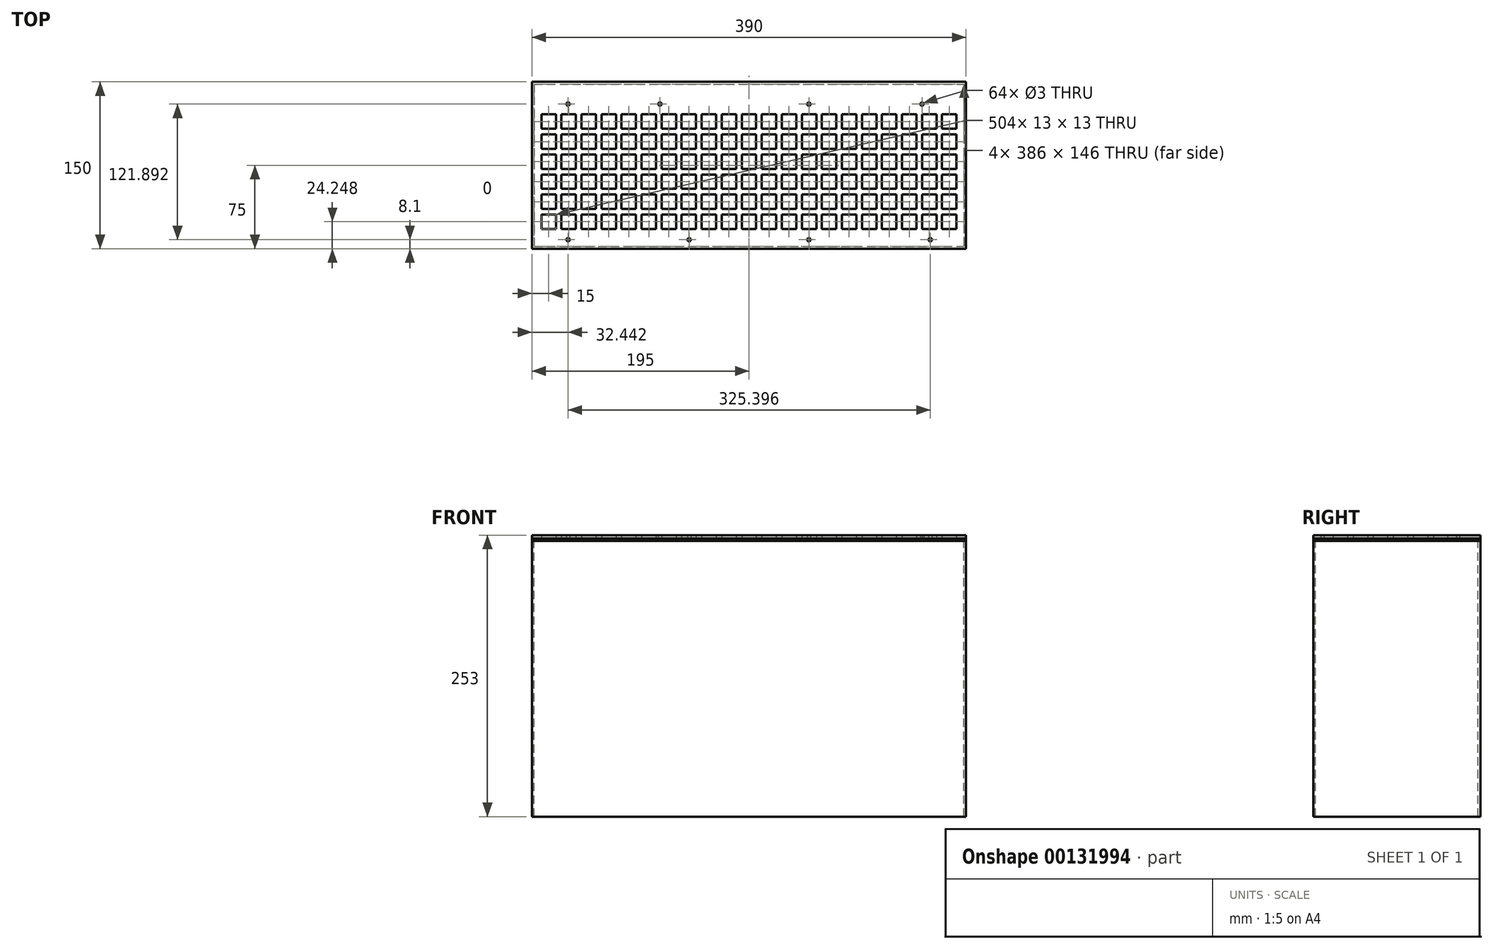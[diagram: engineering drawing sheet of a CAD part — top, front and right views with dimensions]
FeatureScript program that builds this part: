
annotation { "Feature Type Name" : "Feature", "Feature Type Description" : "" }
export const myFeature = defineFeature(function(context is Context, id is Id, definition is map)
    precondition{}
    {
        {
            var Q0;
            Q0=qCreatedBy(makeId("Top.planeOp"),FACE);
            var sketch = newSketch(context, id + "F0", { "sketchPlane" : qUnion([Q0])});
            skLineSegment(sketch, "E0.bottom", {"start": v(0, 0) * mm, "end": v(390, 0) * mm});
            skLineSegment(sketch, "E0.top", {"start": v(0, -150) * mm, "end": v(390, -150) * mm});
            skLineSegment(sketch, "E0.left", {"start": v(0, 0) * mm, "end": v(0, -150) * mm});
            skLineSegment(sketch, "E0.right", {"start": v(390, 0) * mm, "end": v(390, -150) * mm});
            skLineSegment(sketch, "E1.bottom", {"start": v(8.5, -29.25) * mm, "end": v(21.5, -29.25) * mm});
            skLineSegment(sketch, "E1.top", {"start": v(8.5, -42.25) * mm, "end": v(21.5, -42.25) * mm});
            skLineSegment(sketch, "E1.left", {"start": v(8.5, -29.25) * mm, "end": v(8.5, -42.25) * mm});
            skLineSegment(sketch, "E1.right", {"start": v(21.5, -29.25) * mm, "end": v(21.5, -42.25) * mm});
            skLineSegment(sketch, "E2.bottom", {"start": v(8.5, -47.25) * mm, "end": v(21.5, -47.25) * mm});
            skLineSegment(sketch, "E2.top", {"start": v(8.5, -60.25) * mm, "end": v(21.5, -60.25) * mm});
            skLineSegment(sketch, "E2.left", {"start": v(8.5, -47.25) * mm, "end": v(8.5, -60.25) * mm});
            skLineSegment(sketch, "E2.right", {"start": v(21.5, -47.25) * mm, "end": v(21.5, -60.25) * mm});
            skLineSegment(sketch, "E3.bottom", {"start": v(8.5, -65.25) * mm, "end": v(21.5, -65.25) * mm});
            skLineSegment(sketch, "E3.top", {"start": v(8.5, -78.25) * mm, "end": v(21.5, -78.25) * mm});
            skLineSegment(sketch, "E3.left", {"start": v(8.5, -65.25) * mm, "end": v(8.5, -78.25) * mm});
            skLineSegment(sketch, "E3.right", {"start": v(21.5, -65.25) * mm, "end": v(21.5, -78.25) * mm});
            skLineSegment(sketch, "E4.bottom", {"start": v(8.5, -83.25) * mm, "end": v(21.5, -83.25) * mm});
            skLineSegment(sketch, "E4.top", {"start": v(8.5, -96.25) * mm, "end": v(21.5, -96.25) * mm});
            skLineSegment(sketch, "E4.left", {"start": v(8.5, -83.25) * mm, "end": v(8.5, -96.25) * mm});
            skLineSegment(sketch, "E4.right", {"start": v(21.5, -83.25) * mm, "end": v(21.5, -96.25) * mm});
            skLineSegment(sketch, "E5.bottom", {"start": v(8.5, -101.25) * mm, "end": v(21.5, -101.25) * mm});
            skLineSegment(sketch, "E5.top", {"start": v(8.5, -114.25) * mm, "end": v(21.5, -114.25) * mm});
            skLineSegment(sketch, "E5.left", {"start": v(8.5, -101.25) * mm, "end": v(8.5, -114.25) * mm});
            skLineSegment(sketch, "E5.right", {"start": v(21.5, -101.25) * mm, "end": v(21.5, -114.25) * mm});
            skLineSegment(sketch, "E6.bottom", {"start": v(8.5, -119.25) * mm, "end": v(21.5, -119.25) * mm});
            skLineSegment(sketch, "E6.top", {"start": v(8.5, -132.25) * mm, "end": v(21.5, -132.25) * mm});
            skLineSegment(sketch, "E6.left", {"start": v(8.5, -119.25) * mm, "end": v(8.5, -132.25) * mm});
            skLineSegment(sketch, "E6.right", {"start": v(21.5, -119.25) * mm, "end": v(21.5, -132.25) * mm});
            skLineSegment(sketch, "E7", {"start": v(24, -21.56) * mm, "end": v(24, -144.75) * mm, "construction": true});
            skLineSegment(sketch, "E8.MirrorCS", {"start": v(39.5, -47.25) * mm, "end": v(39.5, -60.25) * mm});
            skLineSegment(sketch, "E9.MirrorCS", {"start": v(39.5, -60.25) * mm, "end": v(26.5, -60.25) * mm});
            skLineSegment(sketch, "E10.MirrorCS", {"start": v(39.5, -132.25) * mm, "end": v(26.5, -132.25) * mm});
            skLineSegment(sketch, "E11.MirrorCS", {"start": v(39.5, -119.25) * mm, "end": v(26.5, -119.25) * mm});
            skLineSegment(sketch, "E12.MirrorCS", {"start": v(39.5, -119.25) * mm, "end": v(39.5, -132.25) * mm});
            skLineSegment(sketch, "E13.MirrorCS", {"start": v(26.5, -29.25) * mm, "end": v(26.5, -42.25) * mm});
            skLineSegment(sketch, "E14.MirrorCS", {"start": v(39.5, -29.25) * mm, "end": v(26.5, -29.25) * mm});
            skLineSegment(sketch, "E15.MirrorCS", {"start": v(39.5, -101.25) * mm, "end": v(26.5, -101.25) * mm});
            skLineSegment(sketch, "E16.MirrorCS", {"start": v(26.5, -83.25) * mm, "end": v(26.5, -96.25) * mm});
            skLineSegment(sketch, "E17.MirrorCS", {"start": v(39.5, -83.25) * mm, "end": v(39.5, -96.25) * mm});
            skLineSegment(sketch, "E18.MirrorCS", {"start": v(39.5, -96.25) * mm, "end": v(26.5, -96.25) * mm});
            skLineSegment(sketch, "E19.MirrorCS", {"start": v(39.5, -83.25) * mm, "end": v(26.5, -83.25) * mm});
            skLineSegment(sketch, "E20.MirrorCS", {"start": v(26.5, -65.25) * mm, "end": v(26.5, -78.25) * mm});
            skLineSegment(sketch, "E21.MirrorCS", {"start": v(39.5, -65.25) * mm, "end": v(39.5, -78.25) * mm});
            skLineSegment(sketch, "E22.MirrorCS", {"start": v(39.5, -65.25) * mm, "end": v(26.5, -65.25) * mm});
            skLineSegment(sketch, "E23.MirrorCS", {"start": v(39.5, -78.25) * mm, "end": v(26.5, -78.25) * mm});
            skLineSegment(sketch, "E24.MirrorCS", {"start": v(26.5, -101.25) * mm, "end": v(26.5, -114.25) * mm});
            skLineSegment(sketch, "E25.MirrorCS", {"start": v(26.5, -47.25) * mm, "end": v(26.5, -60.25) * mm});
            skLineSegment(sketch, "E26.MirrorCS", {"start": v(26.5, -119.25) * mm, "end": v(26.5, -132.25) * mm});
            skLineSegment(sketch, "E27.MirrorCS", {"start": v(39.5, -101.25) * mm, "end": v(39.5, -114.25) * mm});
            skLineSegment(sketch, "E28.MirrorCS", {"start": v(39.5, -29.25) * mm, "end": v(39.5, -42.25) * mm});
            skLineSegment(sketch, "E29.MirrorCS", {"start": v(39.5, -114.25) * mm, "end": v(26.5, -114.25) * mm});
            skLineSegment(sketch, "E30.MirrorCS", {"start": v(39.5, -47.25) * mm, "end": v(26.5, -47.25) * mm});
            skLineSegment(sketch, "E31.MirrorCS", {"start": v(39.5, -42.25) * mm, "end": v(26.5, -42.25) * mm});
            skLineSegment(sketch, "E32", {"start": v(42, -21.56) * mm, "end": v(42, -144.75) * mm, "construction": true});
            skLineSegment(sketch, "E33.MirrorCS", {"start": v(57.5, -119.25) * mm, "end": v(57.5, -132.25) * mm});
            skLineSegment(sketch, "E34.MirrorCS", {"start": v(44.5, -29.25) * mm, "end": v(44.5, -42.25) * mm});
            skLineSegment(sketch, "E35.MirrorCS", {"start": v(44.5, -119.25) * mm, "end": v(44.5, -132.25) * mm});
            skLineSegment(sketch, "E36.MirrorCS", {"start": v(44.5, -114.25) * mm, "end": v(57.5, -114.25) * mm});
            skLineSegment(sketch, "E37.MirrorCS", {"start": v(75.5, -83.25) * mm, "end": v(75.5, -96.25) * mm});
            skLineSegment(sketch, "E38.MirrorCS", {"start": v(62.5, -65.25) * mm, "end": v(62.5, -78.25) * mm});
            skLineSegment(sketch, "E39.MirrorCS", {"start": v(75.5, -114.25) * mm, "end": v(62.5, -114.25) * mm});
            skLineSegment(sketch, "E40.MirrorCS", {"start": v(75.5, -42.25) * mm, "end": v(62.5, -42.25) * mm});
            skLineSegment(sketch, "E41.MirrorCS", {"start": v(57.5, -83.25) * mm, "end": v(57.5, -96.25) * mm});
            skLineSegment(sketch, "E42.MirrorCS", {"start": v(75.5, -101.25) * mm, "end": v(75.5, -114.25) * mm});
            skLineSegment(sketch, "E43.MirrorCS", {"start": v(75.5, -29.25) * mm, "end": v(75.5, -42.25) * mm});
            skLineSegment(sketch, "E44.MirrorCS", {"start": v(44.5, -83.25) * mm, "end": v(44.5, -96.25) * mm});
            skLineSegment(sketch, "E45.MirrorCS", {"start": v(44.5, -96.25) * mm, "end": v(57.5, -96.25) * mm});
            skLineSegment(sketch, "E46.MirrorCS", {"start": v(62.5, -101.25) * mm, "end": v(62.5, -114.25) * mm});
            skLineSegment(sketch, "E47.MirrorCS", {"start": v(62.5, -29.25) * mm, "end": v(62.5, -42.25) * mm});
            skLineSegment(sketch, "E48.MirrorCS", {"start": v(44.5, -83.25) * mm, "end": v(57.5, -83.25) * mm});
            skLineSegment(sketch, "E49.MirrorCS", {"start": v(75.5, -119.25) * mm, "end": v(62.5, -119.25) * mm});
            skLineSegment(sketch, "E50.MirrorCS", {"start": v(75.5, -47.25) * mm, "end": v(62.5, -47.25) * mm});
            skLineSegment(sketch, "E51.MirrorCS", {"start": v(57.5, -65.25) * mm, "end": v(57.5, -78.25) * mm});
            skLineSegment(sketch, "E52.MirrorCS", {"start": v(75.5, -60.25) * mm, "end": v(62.5, -60.25) * mm});
            skLineSegment(sketch, "E53.MirrorCS", {"start": v(75.5, -132.25) * mm, "end": v(62.5, -132.25) * mm});
            skLineSegment(sketch, "E54.MirrorCS", {"start": v(44.5, -132.25) * mm, "end": v(57.5, -132.25) * mm});
            skLineSegment(sketch, "E55.MirrorCS", {"start": v(75.5, -78.25) * mm, "end": v(62.5, -78.25) * mm});
            skLineSegment(sketch, "E56.MirrorCS", {"start": v(57.5, -101.25) * mm, "end": v(57.5, -114.25) * mm});
            skLineSegment(sketch, "E57.MirrorCS", {"start": v(44.5, -47.25) * mm, "end": v(44.5, -60.25) * mm});
            skLineSegment(sketch, "E58.MirrorCS", {"start": v(44.5, -65.25) * mm, "end": v(44.5, -78.25) * mm});
            skLineSegment(sketch, "E59.MirrorCS", {"start": v(75.5, -119.25) * mm, "end": v(75.5, -132.25) * mm});
            skLineSegment(sketch, "E60.MirrorCS", {"start": v(75.5, -47.25) * mm, "end": v(75.5, -60.25) * mm});
            skLineSegment(sketch, "E61.MirrorCS", {"start": v(75.5, -65.25) * mm, "end": v(75.5, -78.25) * mm});
            skLineSegment(sketch, "E62.MirrorCS", {"start": v(57.5, -47.25) * mm, "end": v(57.5, -60.25) * mm});
            skLineSegment(sketch, "E63.MirrorCS", {"start": v(44.5, -60.25) * mm, "end": v(57.5, -60.25) * mm});
            skLineSegment(sketch, "E64.MirrorCS", {"start": v(44.5, -65.25) * mm, "end": v(57.5, -65.25) * mm});
            skLineSegment(sketch, "E65.MirrorCS", {"start": v(62.5, -119.25) * mm, "end": v(62.5, -132.25) * mm});
            skLineSegment(sketch, "E66.MirrorCS", {"start": v(62.5, -47.25) * mm, "end": v(62.5, -60.25) * mm});
            skLineSegment(sketch, "E67.MirrorCS", {"start": v(44.5, -119.25) * mm, "end": v(57.5, -119.25) * mm});
            skLineSegment(sketch, "E68.MirrorCS", {"start": v(44.5, -101.25) * mm, "end": v(44.5, -114.25) * mm});
            skLineSegment(sketch, "E69.MirrorCS", {"start": v(75.5, -83.25) * mm, "end": v(62.5, -83.25) * mm});
            skLineSegment(sketch, "E70.MirrorCS", {"start": v(44.5, -101.25) * mm, "end": v(57.5, -101.25) * mm});
            skLineSegment(sketch, "E71.MirrorCS", {"start": v(75.5, -96.25) * mm, "end": v(62.5, -96.25) * mm});
            skLineSegment(sketch, "E72.MirrorCS", {"start": v(44.5, -78.25) * mm, "end": v(57.5, -78.25) * mm});
            skLineSegment(sketch, "E73.MirrorCS", {"start": v(75.5, -65.25) * mm, "end": v(62.5, -65.25) * mm});
            skLineSegment(sketch, "E74.MirrorCS", {"start": v(44.5, -42.25) * mm, "end": v(57.5, -42.25) * mm});
            skLineSegment(sketch, "E75.MirrorCS", {"start": v(44.5, -47.25) * mm, "end": v(57.5, -47.25) * mm});
            skLineSegment(sketch, "E76.MirrorCS", {"start": v(62.5, -83.25) * mm, "end": v(62.5, -96.25) * mm});
            skLineSegment(sketch, "E77.MirrorCS", {"start": v(75.5, -29.25) * mm, "end": v(62.5, -29.25) * mm});
            skLineSegment(sketch, "E78.MirrorCS", {"start": v(44.5, -29.25) * mm, "end": v(57.5, -29.25) * mm});
            skLineSegment(sketch, "E79.MirrorCS", {"start": v(75.5, -101.25) * mm, "end": v(62.5, -101.25) * mm});
            skLineSegment(sketch, "E80.MirrorCS", {"start": v(57.5, -29.25) * mm, "end": v(57.5, -42.25) * mm});
            skLineSegment(sketch, "E81", {"start": v(78, -21.56) * mm, "end": v(78, -144.75) * mm, "construction": true});
            skLineSegment(sketch, "E82.MirrorCS", {"start": v(111.5, -29.25) * mm, "end": v(111.5, -42.25) * mm});
            skLineSegment(sketch, "E83.MirrorCS", {"start": v(116.5, -83.25) * mm, "end": v(116.5, -96.25) * mm});
            skLineSegment(sketch, "E84.MirrorCS", {"start": v(93.5, -119.25) * mm, "end": v(93.5, -132.25) * mm});
            skLineSegment(sketch, "E85.MirrorCS", {"start": v(147.5, -47.25) * mm, "end": v(134.5, -47.25) * mm});
            skLineSegment(sketch, "E86.MirrorCS", {"start": v(147.5, -101.25) * mm, "end": v(134.5, -101.25) * mm});
            skLineSegment(sketch, "E87.MirrorCS", {"start": v(147.5, -29.25) * mm, "end": v(134.5, -29.25) * mm});
            skLineSegment(sketch, "E88.MirrorCS", {"start": v(147.5, -119.25) * mm, "end": v(134.5, -119.25) * mm});
            skLineSegment(sketch, "E89.MirrorCS", {"start": v(116.5, -83.25) * mm, "end": v(129.5, -83.25) * mm});
            skLineSegment(sketch, "E90.MirrorCS", {"start": v(111.5, -119.25) * mm, "end": v(111.5, -132.25) * mm});
            skLineSegment(sketch, "E91.MirrorCS", {"start": v(98.5, -29.25) * mm, "end": v(98.5, -42.25) * mm});
            skLineSegment(sketch, "E92.MirrorCS", {"start": v(129.5, -83.25) * mm, "end": v(129.5, -96.25) * mm});
            skLineSegment(sketch, "E93.MirrorCS", {"start": v(147.5, -65.25) * mm, "end": v(147.5, -78.25) * mm});
            skLineSegment(sketch, "E94.MirrorCS", {"start": v(116.5, -29.25) * mm, "end": v(129.5, -29.25) * mm});
            skLineSegment(sketch, "E95.MirrorCS", {"start": v(116.5, -47.25) * mm, "end": v(129.5, -47.25) * mm});
            skLineSegment(sketch, "E96.MirrorCS", {"start": v(93.5, -101.25) * mm, "end": v(93.5, -114.25) * mm});
            skLineSegment(sketch, "E97.MirrorCS", {"start": v(98.5, -47.25) * mm, "end": v(98.5, -60.25) * mm});
            skLineSegment(sketch, "E98.MirrorCS", {"start": v(93.5, -47.25) * mm, "end": v(93.5, -60.25) * mm});
            skLineSegment(sketch, "E99.MirrorCS", {"start": v(134.5, -83.25) * mm, "end": v(134.5, -96.25) * mm});
            skLineSegment(sketch, "E100.MirrorCS", {"start": v(111.5, -29.25) * mm, "end": v(98.5, -29.25) * mm});
            skLineSegment(sketch, "E101.MirrorCS", {"start": v(80.5, -29.25) * mm, "end": v(93.5, -29.25) * mm});
            skLineSegment(sketch, "E102.MirrorCS", {"start": v(129.5, -29.25) * mm, "end": v(129.5, -42.25) * mm});
            skLineSegment(sketch, "E103.MirrorCS", {"start": v(116.5, -114.25) * mm, "end": v(129.5, -114.25) * mm});
            skLineSegment(sketch, "E104.MirrorCS", {"start": v(111.5, -96.25) * mm, "end": v(98.5, -96.25) * mm});
            skLineSegment(sketch, "E105.MirrorCS", {"start": v(80.5, -65.25) * mm, "end": v(80.5, -78.25) * mm});
            skLineSegment(sketch, "E106.MirrorCS", {"start": v(93.5, -83.25) * mm, "end": v(93.5, -96.25) * mm});
            skLineSegment(sketch, "E107.MirrorCS", {"start": v(116.5, -119.25) * mm, "end": v(116.5, -132.25) * mm});
            skLineSegment(sketch, "E108.MirrorCS", {"start": v(116.5, -29.25) * mm, "end": v(116.5, -42.25) * mm});
            skLineSegment(sketch, "E109.MirrorCS", {"start": v(111.5, -83.25) * mm, "end": v(111.5, -96.25) * mm});
            skLineSegment(sketch, "E110.MirrorCS", {"start": v(80.5, -47.25) * mm, "end": v(80.5, -60.25) * mm});
            skLineSegment(sketch, "E111.MirrorCS", {"start": v(147.5, -96.25) * mm, "end": v(134.5, -96.25) * mm});
            skLineSegment(sketch, "E112.MirrorCS", {"start": v(134.5, -29.25) * mm, "end": v(134.5, -42.25) * mm});
            skLineSegment(sketch, "E113.MirrorCS", {"start": v(80.5, -132.25) * mm, "end": v(93.5, -132.25) * mm});
            skLineSegment(sketch, "E114.MirrorCS", {"start": v(80.5, -83.25) * mm, "end": v(93.5, -83.25) * mm});
            skLineSegment(sketch, "E115.MirrorCS", {"start": v(147.5, -47.25) * mm, "end": v(147.5, -60.25) * mm});
            skLineSegment(sketch, "E116.MirrorCS", {"start": v(147.5, -119.25) * mm, "end": v(147.5, -132.25) * mm});
            skLineSegment(sketch, "E117.MirrorCS", {"start": v(116.5, -65.25) * mm, "end": v(116.5, -78.25) * mm});
            skLineSegment(sketch, "E118.MirrorCS", {"start": v(80.5, -83.25) * mm, "end": v(80.5, -96.25) * mm});
            skLineSegment(sketch, "E119.MirrorCS", {"start": v(134.5, -101.25) * mm, "end": v(134.5, -114.25) * mm});
            skLineSegment(sketch, "E120.MirrorCS", {"start": v(111.5, -47.25) * mm, "end": v(98.5, -47.25) * mm});
            skLineSegment(sketch, "E121.MirrorCS", {"start": v(116.5, -101.25) * mm, "end": v(116.5, -114.25) * mm});
            skLineSegment(sketch, "E122.MirrorCS", {"start": v(116.5, -119.25) * mm, "end": v(129.5, -119.25) * mm});
            skLineSegment(sketch, "E123.MirrorCS", {"start": v(80.5, -29.25) * mm, "end": v(80.5, -42.25) * mm});
            skLineSegment(sketch, "E124.MirrorCS", {"start": v(80.5, -119.25) * mm, "end": v(80.5, -132.25) * mm});
            skLineSegment(sketch, "E125.MirrorCS", {"start": v(147.5, -83.25) * mm, "end": v(134.5, -83.25) * mm});
            skLineSegment(sketch, "E126.MirrorCS", {"start": v(111.5, -42.25) * mm, "end": v(98.5, -42.25) * mm});
            skLineSegment(sketch, "E127.MirrorCS", {"start": v(116.5, -132.25) * mm, "end": v(129.5, -132.25) * mm});
            skLineSegment(sketch, "E128.MirrorCS", {"start": v(129.5, -119.25) * mm, "end": v(129.5, -132.25) * mm});
            skLineSegment(sketch, "E129.MirrorCS", {"start": v(80.5, -101.25) * mm, "end": v(80.5, -114.25) * mm});
            skLineSegment(sketch, "E130.MirrorCS", {"start": v(111.5, -65.25) * mm, "end": v(111.5, -78.25) * mm});
            skLineSegment(sketch, "E131.MirrorCS", {"start": v(80.5, -60.25) * mm, "end": v(93.5, -60.25) * mm});
            skLineSegment(sketch, "E132.MirrorCS", {"start": v(111.5, -101.25) * mm, "end": v(111.5, -114.25) * mm});
            skLineSegment(sketch, "E133.MirrorCS", {"start": v(134.5, -65.25) * mm, "end": v(134.5, -78.25) * mm});
            skLineSegment(sketch, "E134.MirrorCS", {"start": v(147.5, -60.25) * mm, "end": v(134.5, -60.25) * mm});
            skLineSegment(sketch, "E135.MirrorCS", {"start": v(147.5, -132.25) * mm, "end": v(134.5, -132.25) * mm});
            skLineSegment(sketch, "E136.MirrorCS", {"start": v(129.5, -65.25) * mm, "end": v(129.5, -78.25) * mm});
            skLineSegment(sketch, "E137.MirrorCS", {"start": v(111.5, -114.25) * mm, "end": v(98.5, -114.25) * mm});
            skLineSegment(sketch, "E138.MirrorCS", {"start": v(80.5, -65.25) * mm, "end": v(93.5, -65.25) * mm});
            skLineSegment(sketch, "E139.MirrorCS", {"start": v(116.5, -60.25) * mm, "end": v(129.5, -60.25) * mm});
            skLineSegment(sketch, "E140.MirrorCS", {"start": v(129.5, -47.25) * mm, "end": v(129.5, -60.25) * mm});
            skLineSegment(sketch, "E141.MirrorCS", {"start": v(98.5, -83.25) * mm, "end": v(98.5, -96.25) * mm});
            skLineSegment(sketch, "E142.MirrorCS", {"start": v(111.5, -47.25) * mm, "end": v(111.5, -60.25) * mm});
            skLineSegment(sketch, "E143.MirrorCS", {"start": v(80.5, -47.25) * mm, "end": v(93.5, -47.25) * mm});
            skLineSegment(sketch, "E144.MirrorCS", {"start": v(116.5, -96.25) * mm, "end": v(129.5, -96.25) * mm});
            skLineSegment(sketch, "E145.MirrorCS", {"start": v(111.5, -119.25) * mm, "end": v(98.5, -119.25) * mm});
            skLineSegment(sketch, "E146.MirrorCS", {"start": v(98.5, -65.25) * mm, "end": v(98.5, -78.25) * mm});
            skLineSegment(sketch, "E147.MirrorCS", {"start": v(111.5, -60.25) * mm, "end": v(98.5, -60.25) * mm});
            skLineSegment(sketch, "E148.MirrorCS", {"start": v(147.5, -83.25) * mm, "end": v(147.5, -96.25) * mm});
            skLineSegment(sketch, "E149.MirrorCS", {"start": v(111.5, -65.25) * mm, "end": v(98.5, -65.25) * mm});
            skLineSegment(sketch, "E150.MirrorCS", {"start": v(111.5, -83.25) * mm, "end": v(98.5, -83.25) * mm});
            skLineSegment(sketch, "E151.MirrorCS", {"start": v(116.5, -42.25) * mm, "end": v(129.5, -42.25) * mm});
            skLineSegment(sketch, "E152.MirrorCS", {"start": v(147.5, -42.25) * mm, "end": v(134.5, -42.25) * mm});
            skLineSegment(sketch, "E153.MirrorCS", {"start": v(147.5, -114.25) * mm, "end": v(134.5, -114.25) * mm});
            skLineSegment(sketch, "E154.MirrorCS", {"start": v(98.5, -101.25) * mm, "end": v(98.5, -114.25) * mm});
            skLineSegment(sketch, "E155.MirrorCS", {"start": v(80.5, -42.25) * mm, "end": v(93.5, -42.25) * mm});
            skLineSegment(sketch, "E156.MirrorCS", {"start": v(129.5, -101.25) * mm, "end": v(129.5, -114.25) * mm});
            skLineSegment(sketch, "E157.MirrorCS", {"start": v(116.5, -47.25) * mm, "end": v(116.5, -60.25) * mm});
            skLineSegment(sketch, "E158.MirrorCS", {"start": v(111.5, -78.25) * mm, "end": v(98.5, -78.25) * mm});
            skLineSegment(sketch, "E159.MirrorCS", {"start": v(147.5, -101.25) * mm, "end": v(147.5, -114.25) * mm});
            skLineSegment(sketch, "E160.MirrorCS", {"start": v(93.5, -29.25) * mm, "end": v(93.5, -42.25) * mm});
            skLineSegment(sketch, "E161.MirrorCS", {"start": v(116.5, -101.25) * mm, "end": v(129.5, -101.25) * mm});
            skLineSegment(sketch, "E162.MirrorCS", {"start": v(80.5, -101.25) * mm, "end": v(93.5, -101.25) * mm});
            skLineSegment(sketch, "E163.MirrorCS", {"start": v(147.5, -29.25) * mm, "end": v(147.5, -42.25) * mm});
            skLineSegment(sketch, "E164.MirrorCS", {"start": v(80.5, -119.25) * mm, "end": v(93.5, -119.25) * mm});
            skLineSegment(sketch, "E165.MirrorCS", {"start": v(98.5, -119.25) * mm, "end": v(98.5, -132.25) * mm});
            skLineSegment(sketch, "E166.MirrorCS", {"start": v(147.5, -78.25) * mm, "end": v(134.5, -78.25) * mm});
            skLineSegment(sketch, "E167.MirrorCS", {"start": v(147.5, -65.25) * mm, "end": v(134.5, -65.25) * mm});
            skLineSegment(sketch, "E168.MirrorCS", {"start": v(80.5, -78.25) * mm, "end": v(93.5, -78.25) * mm});
            skLineSegment(sketch, "E169.MirrorCS", {"start": v(80.5, -96.25) * mm, "end": v(93.5, -96.25) * mm});
            skLineSegment(sketch, "E170.MirrorCS", {"start": v(116.5, -78.25) * mm, "end": v(129.5, -78.25) * mm});
            skLineSegment(sketch, "E171.MirrorCS", {"start": v(80.5, -114.25) * mm, "end": v(93.5, -114.25) * mm});
            skLineSegment(sketch, "E172.MirrorCS", {"start": v(134.5, -119.25) * mm, "end": v(134.5, -132.25) * mm});
            skLineSegment(sketch, "E173.MirrorCS", {"start": v(116.5, -65.25) * mm, "end": v(129.5, -65.25) * mm});
            skLineSegment(sketch, "E174.MirrorCS", {"start": v(93.5, -65.25) * mm, "end": v(93.5, -78.25) * mm});
            skLineSegment(sketch, "E175.MirrorCS", {"start": v(134.5, -47.25) * mm, "end": v(134.5, -60.25) * mm});
            skLineSegment(sketch, "E176.MirrorCS", {"start": v(111.5, -101.25) * mm, "end": v(98.5, -101.25) * mm});
            skLineSegment(sketch, "E177.MirrorCS", {"start": v(111.5, -132.25) * mm, "end": v(98.5, -132.25) * mm});
            skLineSegment(sketch, "E178", {"start": v(150, -21.56) * mm, "end": v(150, -144.75) * mm, "construction": true});
            skLineSegment(sketch, "E179.MirrorCS", {"start": v(291.5, -83.25) * mm, "end": v(291.5, -96.25) * mm});
            skLineSegment(sketch, "E180.MirrorCS", {"start": v(291.5, -101.25) * mm, "end": v(278.5, -101.25) * mm});
            skLineSegment(sketch, "E181.MirrorCS", {"start": v(291.5, -29.25) * mm, "end": v(278.5, -29.25) * mm});
            skLineSegment(sketch, "E182.MirrorCS", {"start": v(291.5, -29.25) * mm, "end": v(291.5, -42.25) * mm});
            skLineSegment(sketch, "E183.MirrorCS", {"start": v(291.5, -47.25) * mm, "end": v(291.5, -60.25) * mm});
            skLineSegment(sketch, "E184.MirrorCS", {"start": v(291.5, -119.25) * mm, "end": v(291.5, -132.25) * mm});
            skLineSegment(sketch, "E185.MirrorCS", {"start": v(291.5, -65.25) * mm, "end": v(278.5, -65.25) * mm});
            skLineSegment(sketch, "E186.MirrorCS", {"start": v(291.5, -65.25) * mm, "end": v(291.5, -78.25) * mm});
            skLineSegment(sketch, "E187.MirrorCS", {"start": v(260.5, -119.25) * mm, "end": v(260.5, -132.25) * mm});
            skLineSegment(sketch, "E188.MirrorCS", {"start": v(255.5, -83.25) * mm, "end": v(255.5, -96.25) * mm});
            skLineSegment(sketch, "E189.MirrorCS", {"start": v(170.5, -101.25) * mm, "end": v(170.5, -114.25) * mm});
            skLineSegment(sketch, "E190.MirrorCS", {"start": v(224.5, -65.25) * mm, "end": v(224.5, -78.25) * mm});
            skLineSegment(sketch, "E191.MirrorCS", {"start": v(255.5, -96.25) * mm, "end": v(242.5, -96.25) * mm});
            skLineSegment(sketch, "E192.MirrorCS", {"start": v(260.5, -114.25) * mm, "end": v(273.5, -114.25) * mm});
            skLineSegment(sketch, "E193.MirrorCS", {"start": v(273.5, -29.25) * mm, "end": v(273.5, -42.25) * mm});
            skLineSegment(sketch, "E194.MirrorCS", {"start": v(152.5, -83.25) * mm, "end": v(165.5, -83.25) * mm});
            skLineSegment(sketch, "E195.MirrorCS", {"start": v(152.5, -65.25) * mm, "end": v(152.5, -78.25) * mm});
            skLineSegment(sketch, "E196.MirrorCS", {"start": v(224.5, -29.25) * mm, "end": v(237.5, -29.25) * mm});
            skLineSegment(sketch, "E197.MirrorCS", {"start": v(183.5, -47.25) * mm, "end": v(183.5, -60.25) * mm});
            skLineSegment(sketch, "E198.MirrorCS", {"start": v(152.5, -101.25) * mm, "end": v(152.5, -114.25) * mm});
            skLineSegment(sketch, "E199.MirrorCS", {"start": v(219.5, -47.25) * mm, "end": v(206.5, -47.25) * mm});
            skLineSegment(sketch, "E200.MirrorCS", {"start": v(219.5, -119.25) * mm, "end": v(219.5, -132.25) * mm});
            skLineSegment(sketch, "E201.MirrorCS", {"start": v(237.5, -29.25) * mm, "end": v(237.5, -42.25) * mm});
            skLineSegment(sketch, "E202.MirrorCS", {"start": v(260.5, -42.25) * mm, "end": v(273.5, -42.25) * mm});
            skLineSegment(sketch, "E203.MirrorCS", {"start": v(260.5, -101.25) * mm, "end": v(273.5, -101.25) * mm});
            skLineSegment(sketch, "E204.MirrorCS", {"start": v(183.5, -132.25) * mm, "end": v(170.5, -132.25) * mm});
            skLineSegment(sketch, "E205.MirrorCS", {"start": v(152.5, -96.25) * mm, "end": v(165.5, -96.25) * mm});
            skLineSegment(sketch, "E206.MirrorCS", {"start": v(183.5, -47.25) * mm, "end": v(170.5, -47.25) * mm});
            skLineSegment(sketch, "E207.MirrorCS", {"start": v(224.5, -101.25) * mm, "end": v(237.5, -101.25) * mm});
            skLineSegment(sketch, "E208.MirrorCS", {"start": v(291.5, -114.25) * mm, "end": v(278.5, -114.25) * mm});
            skLineSegment(sketch, "E209.MirrorCS", {"start": v(291.5, -42.25) * mm, "end": v(278.5, -42.25) * mm});
            skLineSegment(sketch, "E210.MirrorCS", {"start": v(255.5, -65.25) * mm, "end": v(242.5, -65.25) * mm});
            skLineSegment(sketch, "E211.MirrorCS", {"start": v(255.5, -83.25) * mm, "end": v(242.5, -83.25) * mm});
            skLineSegment(sketch, "E212.MirrorCS", {"start": v(273.5, -83.25) * mm, "end": v(273.5, -96.25) * mm});
            skLineSegment(sketch, "E213.MirrorCS", {"start": v(165.5, -29.25) * mm, "end": v(165.5, -42.25) * mm});
            skLineSegment(sketch, "E214.MirrorCS", {"start": v(242.5, -29.25) * mm, "end": v(242.5, -42.25) * mm});
            skLineSegment(sketch, "E215.MirrorCS", {"start": v(206.5, -101.25) * mm, "end": v(206.5, -114.25) * mm});
            skLineSegment(sketch, "E216.MirrorCS", {"start": v(188.5, -101.25) * mm, "end": v(201.5, -101.25) * mm});
            skLineSegment(sketch, "E217.MirrorCS", {"start": v(206.5, -29.25) * mm, "end": v(206.5, -42.25) * mm});
            skLineSegment(sketch, "E218.MirrorCS", {"start": v(183.5, -96.25) * mm, "end": v(170.5, -96.25) * mm});
            skLineSegment(sketch, "E219.MirrorCS", {"start": v(291.5, -101.25) * mm, "end": v(291.5, -114.25) * mm});
            skLineSegment(sketch, "E220.MirrorCS", {"start": v(237.5, -119.25) * mm, "end": v(237.5, -132.25) * mm});
            skLineSegment(sketch, "E221.MirrorCS", {"start": v(224.5, -119.25) * mm, "end": v(237.5, -119.25) * mm});
            skLineSegment(sketch, "E222.MirrorCS", {"start": v(242.5, -119.25) * mm, "end": v(242.5, -132.25) * mm});
            skLineSegment(sketch, "E223.MirrorCS", {"start": v(260.5, -83.25) * mm, "end": v(260.5, -96.25) * mm});
            skLineSegment(sketch, "E224.MirrorCS", {"start": v(219.5, -101.25) * mm, "end": v(219.5, -114.25) * mm});
            skLineSegment(sketch, "E225.MirrorCS", {"start": v(219.5, -132.25) * mm, "end": v(206.5, -132.25) * mm});
            skLineSegment(sketch, "E226.MirrorCS", {"start": v(201.5, -47.25) * mm, "end": v(201.5, -60.25) * mm});
            skLineSegment(sketch, "E227.MirrorCS", {"start": v(188.5, -132.25) * mm, "end": v(201.5, -132.25) * mm});
            skLineSegment(sketch, "E228.MirrorCS", {"start": v(183.5, -101.25) * mm, "end": v(170.5, -101.25) * mm});
            skLineSegment(sketch, "E229.MirrorCS", {"start": v(188.5, -119.25) * mm, "end": v(201.5, -119.25) * mm});
            skLineSegment(sketch, "E230.MirrorCS", {"start": v(278.5, -65.25) * mm, "end": v(278.5, -78.25) * mm});
            skLineSegment(sketch, "E231.MirrorCS", {"start": v(255.5, -65.25) * mm, "end": v(255.5, -78.25) * mm});
            skLineSegment(sketch, "E232.MirrorCS", {"start": v(224.5, -101.25) * mm, "end": v(224.5, -114.25) * mm});
            skLineSegment(sketch, "E233.MirrorCS", {"start": v(273.5, -119.25) * mm, "end": v(273.5, -132.25) * mm});
            skLineSegment(sketch, "E234.MirrorCS", {"start": v(260.5, -132.25) * mm, "end": v(273.5, -132.25) * mm});
            skLineSegment(sketch, "E235.MirrorCS", {"start": v(206.5, -83.25) * mm, "end": v(206.5, -96.25) * mm});
            skLineSegment(sketch, "E236.MirrorCS", {"start": v(183.5, -119.25) * mm, "end": v(170.5, -119.25) * mm});
            skLineSegment(sketch, "E237.MirrorCS", {"start": v(170.5, -83.25) * mm, "end": v(170.5, -96.25) * mm});
            skLineSegment(sketch, "E238.MirrorCS", {"start": v(188.5, -119.25) * mm, "end": v(188.5, -132.25) * mm});
            skLineSegment(sketch, "E239.MirrorCS", {"start": v(183.5, -78.25) * mm, "end": v(170.5, -78.25) * mm});
            skLineSegment(sketch, "E240.MirrorCS", {"start": v(255.5, -42.25) * mm, "end": v(242.5, -42.25) * mm});
            skLineSegment(sketch, "E241.MirrorCS", {"start": v(201.5, -101.25) * mm, "end": v(201.5, -114.25) * mm});
            skLineSegment(sketch, "E242.MirrorCS", {"start": v(219.5, -65.25) * mm, "end": v(206.5, -65.25) * mm});
            skLineSegment(sketch, "E243.MirrorCS", {"start": v(255.5, -29.25) * mm, "end": v(255.5, -42.25) * mm});
            skLineSegment(sketch, "E244.MirrorCS", {"start": v(260.5, -96.25) * mm, "end": v(273.5, -96.25) * mm});
            skLineSegment(sketch, "E245.MirrorCS", {"start": v(291.5, -83.25) * mm, "end": v(278.5, -83.25) * mm});
            skLineSegment(sketch, "E246.MirrorCS", {"start": v(278.5, -29.25) * mm, "end": v(278.5, -42.25) * mm});
            skLineSegment(sketch, "E247.MirrorCS", {"start": v(278.5, -101.25) * mm, "end": v(278.5, -114.25) * mm});
            skLineSegment(sketch, "E248.MirrorCS", {"start": v(224.5, -119.25) * mm, "end": v(224.5, -132.25) * mm});
            skLineSegment(sketch, "E249.MirrorCS", {"start": v(224.5, -29.25) * mm, "end": v(224.5, -42.25) * mm});
            skLineSegment(sketch, "E250.MirrorCS", {"start": v(260.5, -101.25) * mm, "end": v(260.5, -114.25) * mm});
            skLineSegment(sketch, "E251.MirrorCS", {"start": v(260.5, -119.25) * mm, "end": v(273.5, -119.25) * mm});
            skLineSegment(sketch, "E252.MirrorCS", {"start": v(219.5, -29.25) * mm, "end": v(219.5, -42.25) * mm});
            skLineSegment(sketch, "E253.MirrorCS", {"start": v(206.5, -47.25) * mm, "end": v(206.5, -60.25) * mm});
            skLineSegment(sketch, "E254.MirrorCS", {"start": v(188.5, -29.25) * mm, "end": v(188.5, -42.25) * mm});
            skLineSegment(sketch, "E255.MirrorCS", {"start": v(237.5, -47.25) * mm, "end": v(237.5, -60.25) * mm});
            skLineSegment(sketch, "E256.MirrorCS", {"start": v(224.5, -47.25) * mm, "end": v(237.5, -47.25) * mm});
            skLineSegment(sketch, "E257.MirrorCS", {"start": v(201.5, -65.25) * mm, "end": v(201.5, -78.25) * mm});
            skLineSegment(sketch, "E258.MirrorCS", {"start": v(219.5, -101.25) * mm, "end": v(206.5, -101.25) * mm});
            skLineSegment(sketch, "E259.MirrorCS", {"start": v(188.5, -65.25) * mm, "end": v(188.5, -78.25) * mm});
            skLineSegment(sketch, "E260.MirrorCS", {"start": v(219.5, -83.25) * mm, "end": v(206.5, -83.25) * mm});
            skLineSegment(sketch, "E261.MirrorCS", {"start": v(183.5, -119.25) * mm, "end": v(183.5, -132.25) * mm});
            skLineSegment(sketch, "E262.MirrorCS", {"start": v(201.5, -29.25) * mm, "end": v(201.5, -42.25) * mm});
            skLineSegment(sketch, "E263.MirrorCS", {"start": v(255.5, -47.25) * mm, "end": v(242.5, -47.25) * mm});
            skLineSegment(sketch, "E264.MirrorCS", {"start": v(219.5, -114.25) * mm, "end": v(206.5, -114.25) * mm});
            skLineSegment(sketch, "E265.MirrorCS", {"start": v(219.5, -42.25) * mm, "end": v(206.5, -42.25) * mm});
            skLineSegment(sketch, "E266.MirrorCS", {"start": v(183.5, -60.25) * mm, "end": v(170.5, -60.25) * mm});
            skLineSegment(sketch, "E267.MirrorCS", {"start": v(170.5, -47.25) * mm, "end": v(170.5, -60.25) * mm});
            skLineSegment(sketch, "E268.MirrorCS", {"start": v(224.5, -47.25) * mm, "end": v(224.5, -60.25) * mm});
            skLineSegment(sketch, "E269.MirrorCS", {"start": v(291.5, -96.25) * mm, "end": v(278.5, -96.25) * mm});
            skLineSegment(sketch, "E270.MirrorCS", {"start": v(219.5, -83.25) * mm, "end": v(219.5, -96.25) * mm});
            skLineSegment(sketch, "E271.MirrorCS", {"start": v(152.5, -60.25) * mm, "end": v(165.5, -60.25) * mm});
            skLineSegment(sketch, "E272.MirrorCS", {"start": v(152.5, -78.25) * mm, "end": v(165.5, -78.25) * mm});
            skLineSegment(sketch, "E273.MirrorCS", {"start": v(188.5, -83.25) * mm, "end": v(201.5, -83.25) * mm});
            skLineSegment(sketch, "E274.MirrorCS", {"start": v(255.5, -101.25) * mm, "end": v(242.5, -101.25) * mm});
            skLineSegment(sketch, "E275.MirrorCS", {"start": v(255.5, -132.25) * mm, "end": v(242.5, -132.25) * mm});
            skLineSegment(sketch, "E276.MirrorCS", {"start": v(152.5, -132.25) * mm, "end": v(165.5, -132.25) * mm});
            skLineSegment(sketch, "E277.MirrorCS", {"start": v(152.5, -101.25) * mm, "end": v(165.5, -101.25) * mm});
            skLineSegment(sketch, "E278.MirrorCS", {"start": v(165.5, -101.25) * mm, "end": v(165.5, -114.25) * mm});
            skLineSegment(sketch, "E279.MirrorCS", {"start": v(170.5, -29.25) * mm, "end": v(170.5, -42.25) * mm});
            skLineSegment(sketch, "E280.MirrorCS", {"start": v(278.5, -47.25) * mm, "end": v(278.5, -60.25) * mm});
            skLineSegment(sketch, "E281.MirrorCS", {"start": v(278.5, -119.25) * mm, "end": v(278.5, -132.25) * mm});
            skLineSegment(sketch, "E282.MirrorCS", {"start": v(260.5, -65.25) * mm, "end": v(273.5, -65.25) * mm});
            skLineSegment(sketch, "E283.MirrorCS", {"start": v(237.5, -65.25) * mm, "end": v(237.5, -78.25) * mm});
            skLineSegment(sketch, "E284.MirrorCS", {"start": v(183.5, -42.25) * mm, "end": v(170.5, -42.25) * mm});
            skLineSegment(sketch, "E285.MirrorCS", {"start": v(165.5, -65.25) * mm, "end": v(165.5, -78.25) * mm});
            skLineSegment(sketch, "E286.MirrorCS", {"start": v(183.5, -65.25) * mm, "end": v(183.5, -78.25) * mm});
            skLineSegment(sketch, "E287.MirrorCS", {"start": v(188.5, -65.25) * mm, "end": v(201.5, -65.25) * mm});
            skLineSegment(sketch, "E288.MirrorCS", {"start": v(201.5, -119.25) * mm, "end": v(201.5, -132.25) * mm});
            skLineSegment(sketch, "E289.MirrorCS", {"start": v(152.5, -65.25) * mm, "end": v(165.5, -65.25) * mm});
            skLineSegment(sketch, "E290.MirrorCS", {"start": v(224.5, -132.25) * mm, "end": v(237.5, -132.25) * mm});
            skLineSegment(sketch, "E291.MirrorCS", {"start": v(224.5, -83.25) * mm, "end": v(237.5, -83.25) * mm});
            skLineSegment(sketch, "E292.MirrorCS", {"start": v(152.5, -47.25) * mm, "end": v(165.5, -47.25) * mm});
            skLineSegment(sketch, "E293.MirrorCS", {"start": v(219.5, -29.25) * mm, "end": v(206.5, -29.25) * mm});
            skLineSegment(sketch, "E294.MirrorCS", {"start": v(260.5, -65.25) * mm, "end": v(260.5, -78.25) * mm});
            skLineSegment(sketch, "E295.MirrorCS", {"start": v(224.5, -83.25) * mm, "end": v(224.5, -96.25) * mm});
            skLineSegment(sketch, "E296.MirrorCS", {"start": v(260.5, -29.25) * mm, "end": v(260.5, -42.25) * mm});
            skLineSegment(sketch, "E297.MirrorCS", {"start": v(188.5, -101.25) * mm, "end": v(188.5, -114.25) * mm});
            skLineSegment(sketch, "E298.MirrorCS", {"start": v(152.5, -119.25) * mm, "end": v(152.5, -132.25) * mm});
            skLineSegment(sketch, "E299.MirrorCS", {"start": v(219.5, -119.25) * mm, "end": v(206.5, -119.25) * mm});
            skLineSegment(sketch, "E300.MirrorCS", {"start": v(152.5, -83.25) * mm, "end": v(152.5, -96.25) * mm});
            skLineSegment(sketch, "E301.MirrorCS", {"start": v(255.5, -101.25) * mm, "end": v(255.5, -114.25) * mm});
            skLineSegment(sketch, "E302.MirrorCS", {"start": v(224.5, -60.25) * mm, "end": v(237.5, -60.25) * mm});
            skLineSegment(sketch, "E303.MirrorCS", {"start": v(188.5, -29.25) * mm, "end": v(201.5, -29.25) * mm});
            skLineSegment(sketch, "E304.MirrorCS", {"start": v(206.5, -119.25) * mm, "end": v(206.5, -132.25) * mm});
            skLineSegment(sketch, "E305.MirrorCS", {"start": v(188.5, -47.25) * mm, "end": v(188.5, -60.25) * mm});
            skLineSegment(sketch, "E306.MirrorCS", {"start": v(188.5, -78.25) * mm, "end": v(201.5, -78.25) * mm});
            skLineSegment(sketch, "E307.MirrorCS", {"start": v(255.5, -29.25) * mm, "end": v(242.5, -29.25) * mm});
            skLineSegment(sketch, "E308.MirrorCS", {"start": v(188.5, -42.25) * mm, "end": v(201.5, -42.25) * mm});
            skLineSegment(sketch, "E309.MirrorCS", {"start": v(206.5, -65.25) * mm, "end": v(206.5, -78.25) * mm});
            skLineSegment(sketch, "E310.MirrorCS", {"start": v(170.5, -119.25) * mm, "end": v(170.5, -132.25) * mm});
            skLineSegment(sketch, "E311.MirrorCS", {"start": v(255.5, -60.25) * mm, "end": v(242.5, -60.25) * mm});
            skLineSegment(sketch, "E312.MirrorCS", {"start": v(165.5, -47.25) * mm, "end": v(165.5, -60.25) * mm});
            skLineSegment(sketch, "E313.MirrorCS", {"start": v(183.5, -29.25) * mm, "end": v(170.5, -29.25) * mm});
            skLineSegment(sketch, "E314.MirrorCS", {"start": v(219.5, -47.25) * mm, "end": v(219.5, -60.25) * mm});
            skLineSegment(sketch, "E315.MirrorCS", {"start": v(183.5, -29.25) * mm, "end": v(183.5, -42.25) * mm});
            skLineSegment(sketch, "E316.MirrorCS", {"start": v(188.5, -60.25) * mm, "end": v(201.5, -60.25) * mm});
            skLineSegment(sketch, "E317.MirrorCS", {"start": v(152.5, -29.25) * mm, "end": v(152.5, -42.25) * mm});
            skLineSegment(sketch, "E318.MirrorCS", {"start": v(242.5, -65.25) * mm, "end": v(242.5, -78.25) * mm});
            skLineSegment(sketch, "E319.MirrorCS", {"start": v(255.5, -119.25) * mm, "end": v(242.5, -119.25) * mm});
            skLineSegment(sketch, "E320.MirrorCS", {"start": v(183.5, -83.25) * mm, "end": v(183.5, -96.25) * mm});
            skLineSegment(sketch, "E321.MirrorCS", {"start": v(291.5, -47.25) * mm, "end": v(278.5, -47.25) * mm});
            skLineSegment(sketch, "E322.MirrorCS", {"start": v(165.5, -83.25) * mm, "end": v(165.5, -96.25) * mm});
            skLineSegment(sketch, "E323.MirrorCS", {"start": v(291.5, -119.25) * mm, "end": v(278.5, -119.25) * mm});
            skLineSegment(sketch, "E324.MirrorCS", {"start": v(260.5, -83.25) * mm, "end": v(273.5, -83.25) * mm});
            skLineSegment(sketch, "E325.MirrorCS", {"start": v(255.5, -119.25) * mm, "end": v(255.5, -132.25) * mm});
            skLineSegment(sketch, "E326.MirrorCS", {"start": v(260.5, -47.25) * mm, "end": v(273.5, -47.25) * mm});
            skLineSegment(sketch, "E327.MirrorCS", {"start": v(224.5, -96.25) * mm, "end": v(237.5, -96.25) * mm});
            skLineSegment(sketch, "E328.MirrorCS", {"start": v(260.5, -29.25) * mm, "end": v(273.5, -29.25) * mm});
            skLineSegment(sketch, "E329.MirrorCS", {"start": v(224.5, -78.25) * mm, "end": v(237.5, -78.25) * mm});
            skLineSegment(sketch, "E330.MirrorCS", {"start": v(201.5, -83.25) * mm, "end": v(201.5, -96.25) * mm});
            skLineSegment(sketch, "E331.MirrorCS", {"start": v(183.5, -65.25) * mm, "end": v(170.5, -65.25) * mm});
            skLineSegment(sketch, "E332.MirrorCS", {"start": v(152.5, -47.25) * mm, "end": v(152.5, -60.25) * mm});
            skLineSegment(sketch, "E333.MirrorCS", {"start": v(219.5, -60.25) * mm, "end": v(206.5, -60.25) * mm});
            skLineSegment(sketch, "E334.MirrorCS", {"start": v(237.5, -83.25) * mm, "end": v(237.5, -96.25) * mm});
            skLineSegment(sketch, "E335.MirrorCS", {"start": v(188.5, -83.25) * mm, "end": v(188.5, -96.25) * mm});
            skLineSegment(sketch, "E336.MirrorCS", {"start": v(237.5, -101.25) * mm, "end": v(237.5, -114.25) * mm});
            skLineSegment(sketch, "E337.MirrorCS", {"start": v(278.5, -83.25) * mm, "end": v(278.5, -96.25) * mm});
            skLineSegment(sketch, "E338.MirrorCS", {"start": v(219.5, -78.25) * mm, "end": v(206.5, -78.25) * mm});
            skLineSegment(sketch, "E339.MirrorCS", {"start": v(152.5, -42.25) * mm, "end": v(165.5, -42.25) * mm});
            skLineSegment(sketch, "E340.MirrorCS", {"start": v(170.5, -65.25) * mm, "end": v(170.5, -78.25) * mm});
            skLineSegment(sketch, "E341.MirrorCS", {"start": v(255.5, -78.25) * mm, "end": v(242.5, -78.25) * mm});
            skLineSegment(sketch, "E342.MirrorCS", {"start": v(255.5, -114.25) * mm, "end": v(242.5, -114.25) * mm});
            skLineSegment(sketch, "E343.MirrorCS", {"start": v(273.5, -65.25) * mm, "end": v(273.5, -78.25) * mm});
            skLineSegment(sketch, "E344.MirrorCS", {"start": v(291.5, -132.25) * mm, "end": v(278.5, -132.25) * mm});
            skLineSegment(sketch, "E345.MirrorCS", {"start": v(291.5, -60.25) * mm, "end": v(278.5, -60.25) * mm});
            skLineSegment(sketch, "E346.MirrorCS", {"start": v(152.5, -119.25) * mm, "end": v(165.5, -119.25) * mm});
            skLineSegment(sketch, "E347.MirrorCS", {"start": v(188.5, -96.25) * mm, "end": v(201.5, -96.25) * mm});
            skLineSegment(sketch, "E348.MirrorCS", {"start": v(242.5, -47.25) * mm, "end": v(242.5, -60.25) * mm});
            skLineSegment(sketch, "E349.MirrorCS", {"start": v(165.5, -119.25) * mm, "end": v(165.5, -132.25) * mm});
            skLineSegment(sketch, "E350.MirrorCS", {"start": v(188.5, -47.25) * mm, "end": v(201.5, -47.25) * mm});
            skLineSegment(sketch, "E351.MirrorCS", {"start": v(260.5, -47.25) * mm, "end": v(260.5, -60.25) * mm});
            skLineSegment(sketch, "E352.MirrorCS", {"start": v(273.5, -101.25) * mm, "end": v(273.5, -114.25) * mm});
            skLineSegment(sketch, "E353.MirrorCS", {"start": v(183.5, -114.25) * mm, "end": v(170.5, -114.25) * mm});
            skLineSegment(sketch, "E354.MirrorCS", {"start": v(152.5, -29.25) * mm, "end": v(165.5, -29.25) * mm});
            skLineSegment(sketch, "E355.MirrorCS", {"start": v(224.5, -42.25) * mm, "end": v(237.5, -42.25) * mm});
            skLineSegment(sketch, "E356.MirrorCS", {"start": v(188.5, -114.25) * mm, "end": v(201.5, -114.25) * mm});
            skLineSegment(sketch, "E357.MirrorCS", {"start": v(291.5, -78.25) * mm, "end": v(278.5, -78.25) * mm});
            skLineSegment(sketch, "E358.MirrorCS", {"start": v(224.5, -114.25) * mm, "end": v(237.5, -114.25) * mm});
            skLineSegment(sketch, "E359.MirrorCS", {"start": v(183.5, -83.25) * mm, "end": v(170.5, -83.25) * mm});
            skLineSegment(sketch, "E360.MirrorCS", {"start": v(273.5, -47.25) * mm, "end": v(273.5, -60.25) * mm});
            skLineSegment(sketch, "E361.MirrorCS", {"start": v(152.5, -114.25) * mm, "end": v(165.5, -114.25) * mm});
            skLineSegment(sketch, "E362.MirrorCS", {"start": v(219.5, -65.25) * mm, "end": v(219.5, -78.25) * mm});
            skLineSegment(sketch, "E363.MirrorCS", {"start": v(255.5, -47.25) * mm, "end": v(255.5, -60.25) * mm});
            skLineSegment(sketch, "E364.MirrorCS", {"start": v(242.5, -83.25) * mm, "end": v(242.5, -96.25) * mm});
            skLineSegment(sketch, "E365.MirrorCS", {"start": v(260.5, -60.25) * mm, "end": v(273.5, -60.25) * mm});
            skLineSegment(sketch, "E366.MirrorCS", {"start": v(224.5, -65.25) * mm, "end": v(237.5, -65.25) * mm});
            skLineSegment(sketch, "E367.MirrorCS", {"start": v(183.5, -101.25) * mm, "end": v(183.5, -114.25) * mm});
            skLineSegment(sketch, "E368.MirrorCS", {"start": v(260.5, -78.25) * mm, "end": v(273.5, -78.25) * mm});
            skLineSegment(sketch, "E369.MirrorCS", {"start": v(219.5, -96.25) * mm, "end": v(206.5, -96.25) * mm});
            skLineSegment(sketch, "E370.MirrorCS", {"start": v(242.5, -101.25) * mm, "end": v(242.5, -114.25) * mm});
            skLineSegment(sketch, "E371", {"start": v(294, -21.56) * mm, "end": v(294, -144.75) * mm, "construction": true});
            skLineSegment(sketch, "E372.MirrorCS", {"start": v(309.5, -83.25) * mm, "end": v(309.5, -96.25) * mm});
            skLineSegment(sketch, "E373.MirrorCS", {"start": v(314.5, -29.25) * mm, "end": v(314.5, -42.25) * mm});
            skLineSegment(sketch, "E374.MirrorCS", {"start": v(327.5, -78.25) * mm, "end": v(314.5, -78.25) * mm});
            skLineSegment(sketch, "E375.MirrorCS", {"start": v(363.5, -47.25) * mm, "end": v(350.5, -47.25) * mm});
            skLineSegment(sketch, "E376.MirrorCS", {"start": v(368.5, -101.25) * mm, "end": v(381.5, -101.25) * mm});
            skLineSegment(sketch, "E377.MirrorCS", {"start": v(368.5, -65.25) * mm, "end": v(381.5, -65.25) * mm});
            skLineSegment(sketch, "E378.MirrorCS", {"start": v(332.5, -65.25) * mm, "end": v(345.5, -65.25) * mm});
            skLineSegment(sketch, "E379.MirrorCS", {"start": v(332.5, -101.25) * mm, "end": v(345.5, -101.25) * mm});
            skLineSegment(sketch, "E380.MirrorCS", {"start": v(363.5, -132.25) * mm, "end": v(350.5, -132.25) * mm});
            skLineSegment(sketch, "E381.MirrorCS", {"start": v(296.5, -119.25) * mm, "end": v(296.5, -132.25) * mm});
            skLineSegment(sketch, "E382.MirrorCS", {"start": v(332.5, -29.25) * mm, "end": v(332.5, -42.25) * mm});
            skLineSegment(sketch, "E383.MirrorCS", {"start": v(296.5, -83.25) * mm, "end": v(296.5, -96.25) * mm});
            skLineSegment(sketch, "E384.MirrorCS", {"start": v(332.5, -83.25) * mm, "end": v(345.5, -83.25) * mm});
            skLineSegment(sketch, "E385.MirrorCS", {"start": v(296.5, -119.25) * mm, "end": v(309.5, -119.25) * mm});
            skLineSegment(sketch, "E386.MirrorCS", {"start": v(332.5, -132.25) * mm, "end": v(345.5, -132.25) * mm});
            skLineSegment(sketch, "E387.MirrorCS", {"start": v(332.5, -29.25) * mm, "end": v(345.5, -29.25) * mm});
            skLineSegment(sketch, "E388.MirrorCS", {"start": v(327.5, -83.25) * mm, "end": v(327.5, -96.25) * mm});
            skLineSegment(sketch, "E389.MirrorCS", {"start": v(363.5, -101.25) * mm, "end": v(350.5, -101.25) * mm});
            skLineSegment(sketch, "E390.MirrorCS", {"start": v(350.5, -47.25) * mm, "end": v(350.5, -60.25) * mm});
            skLineSegment(sketch, "E391.MirrorCS", {"start": v(327.5, -47.25) * mm, "end": v(327.5, -60.25) * mm});
            skLineSegment(sketch, "E392.MirrorCS", {"start": v(332.5, -119.25) * mm, "end": v(345.5, -119.25) * mm});
            skLineSegment(sketch, "E393.MirrorCS", {"start": v(363.5, -29.25) * mm, "end": v(350.5, -29.25) * mm});
            skLineSegment(sketch, "E394.MirrorCS", {"start": v(296.5, -101.25) * mm, "end": v(309.5, -101.25) * mm});
            skLineSegment(sketch, "E395.MirrorCS", {"start": v(368.5, -83.25) * mm, "end": v(381.5, -83.25) * mm});
            skLineSegment(sketch, "E396.MirrorCS", {"start": v(327.5, -96.25) * mm, "end": v(314.5, -96.25) * mm});
            skLineSegment(sketch, "E397.MirrorCS", {"start": v(314.5, -83.25) * mm, "end": v(314.5, -96.25) * mm});
            skLineSegment(sketch, "E398.MirrorCS", {"start": v(327.5, -83.25) * mm, "end": v(314.5, -83.25) * mm});
            skLineSegment(sketch, "E399.MirrorCS", {"start": v(296.5, -114.25) * mm, "end": v(309.5, -114.25) * mm});
            skLineSegment(sketch, "E400.MirrorCS", {"start": v(350.5, -29.25) * mm, "end": v(350.5, -42.25) * mm});
            skLineSegment(sketch, "E401.MirrorCS", {"start": v(381.5, -29.25) * mm, "end": v(381.5, -42.25) * mm});
            skLineSegment(sketch, "E402.MirrorCS", {"start": v(309.5, -119.25) * mm, "end": v(309.5, -132.25) * mm});
            skLineSegment(sketch, "E403.MirrorCS", {"start": v(368.5, -42.25) * mm, "end": v(381.5, -42.25) * mm});
            skLineSegment(sketch, "E404.MirrorCS", {"start": v(363.5, -29.25) * mm, "end": v(363.5, -42.25) * mm});
            skLineSegment(sketch, "E405.MirrorCS", {"start": v(314.5, -119.25) * mm, "end": v(314.5, -132.25) * mm});
            skLineSegment(sketch, "E406.MirrorCS", {"start": v(296.5, -60.25) * mm, "end": v(309.5, -60.25) * mm});
            skLineSegment(sketch, "E407.MirrorCS", {"start": v(314.5, -101.25) * mm, "end": v(314.5, -114.25) * mm});
            skLineSegment(sketch, "E408.MirrorCS", {"start": v(363.5, -78.25) * mm, "end": v(350.5, -78.25) * mm});
            skLineSegment(sketch, "E409.MirrorCS", {"start": v(350.5, -101.25) * mm, "end": v(350.5, -114.25) * mm});
            skLineSegment(sketch, "E410.MirrorCS", {"start": v(296.5, -65.25) * mm, "end": v(309.5, -65.25) * mm});
            skLineSegment(sketch, "E411.MirrorCS", {"start": v(327.5, -65.25) * mm, "end": v(314.5, -65.25) * mm});
            skLineSegment(sketch, "E412.MirrorCS", {"start": v(327.5, -101.25) * mm, "end": v(327.5, -114.25) * mm});
            skLineSegment(sketch, "E413.MirrorCS", {"start": v(327.5, -132.25) * mm, "end": v(314.5, -132.25) * mm});
            skLineSegment(sketch, "E414.MirrorCS", {"start": v(368.5, -47.25) * mm, "end": v(368.5, -60.25) * mm});
            skLineSegment(sketch, "E415.MirrorCS", {"start": v(368.5, -65.25) * mm, "end": v(368.5, -78.25) * mm});
            skLineSegment(sketch, "E416.MirrorCS", {"start": v(296.5, -65.25) * mm, "end": v(296.5, -78.25) * mm});
            skLineSegment(sketch, "E417.MirrorCS", {"start": v(327.5, -42.25) * mm, "end": v(314.5, -42.25) * mm});
            skLineSegment(sketch, "E418.MirrorCS", {"start": v(327.5, -119.25) * mm, "end": v(327.5, -132.25) * mm});
            skLineSegment(sketch, "E419.MirrorCS", {"start": v(327.5, -101.25) * mm, "end": v(314.5, -101.25) * mm});
            skLineSegment(sketch, "E420.MirrorCS", {"start": v(296.5, -101.25) * mm, "end": v(296.5, -114.25) * mm});
            skLineSegment(sketch, "E421.MirrorCS", {"start": v(350.5, -65.25) * mm, "end": v(350.5, -78.25) * mm});
            skLineSegment(sketch, "E422.MirrorCS", {"start": v(381.5, -83.25) * mm, "end": v(381.5, -96.25) * mm});
            skLineSegment(sketch, "E423.MirrorCS", {"start": v(327.5, -119.25) * mm, "end": v(314.5, -119.25) * mm});
            skLineSegment(sketch, "E424.MirrorCS", {"start": v(368.5, -119.25) * mm, "end": v(381.5, -119.25) * mm});
            skLineSegment(sketch, "E425.MirrorCS", {"start": v(332.5, -47.25) * mm, "end": v(332.5, -60.25) * mm});
            skLineSegment(sketch, "E426.MirrorCS", {"start": v(332.5, -83.25) * mm, "end": v(332.5, -96.25) * mm});
            skLineSegment(sketch, "E427.MirrorCS", {"start": v(350.5, -119.25) * mm, "end": v(350.5, -132.25) * mm});
            skLineSegment(sketch, "E428.MirrorCS", {"start": v(363.5, -47.25) * mm, "end": v(363.5, -60.25) * mm});
            skLineSegment(sketch, "E429.MirrorCS", {"start": v(368.5, -29.25) * mm, "end": v(368.5, -42.25) * mm});
            skLineSegment(sketch, "E430.MirrorCS", {"start": v(345.5, -47.25) * mm, "end": v(345.5, -60.25) * mm});
            skLineSegment(sketch, "E431.MirrorCS", {"start": v(314.5, -65.25) * mm, "end": v(314.5, -78.25) * mm});
            skLineSegment(sketch, "E432.MirrorCS", {"start": v(332.5, -60.25) * mm, "end": v(345.5, -60.25) * mm});
            skLineSegment(sketch, "E433.MirrorCS", {"start": v(363.5, -83.25) * mm, "end": v(363.5, -96.25) * mm});
            skLineSegment(sketch, "E434.MirrorCS", {"start": v(381.5, -101.25) * mm, "end": v(381.5, -114.25) * mm});
            skLineSegment(sketch, "E435.MirrorCS", {"start": v(332.5, -47.25) * mm, "end": v(345.5, -47.25) * mm});
            skLineSegment(sketch, "E436.MirrorCS", {"start": v(363.5, -96.25) * mm, "end": v(350.5, -96.25) * mm});
            skLineSegment(sketch, "E437.MirrorCS", {"start": v(332.5, -65.25) * mm, "end": v(332.5, -78.25) * mm});
            skLineSegment(sketch, "E438.MirrorCS", {"start": v(309.5, -101.25) * mm, "end": v(309.5, -114.25) * mm});
            skLineSegment(sketch, "E439.MirrorCS", {"start": v(345.5, -83.25) * mm, "end": v(345.5, -96.25) * mm});
            skLineSegment(sketch, "E440.MirrorCS", {"start": v(296.5, -47.25) * mm, "end": v(296.5, -60.25) * mm});
            skLineSegment(sketch, "E441.MirrorCS", {"start": v(368.5, -119.25) * mm, "end": v(368.5, -132.25) * mm});
            skLineSegment(sketch, "E442.MirrorCS", {"start": v(368.5, -47.25) * mm, "end": v(381.5, -47.25) * mm});
            skLineSegment(sketch, "E443.MirrorCS", {"start": v(381.5, -47.25) * mm, "end": v(381.5, -60.25) * mm});
            skLineSegment(sketch, "E444.MirrorCS", {"start": v(368.5, -60.25) * mm, "end": v(381.5, -60.25) * mm});
            skLineSegment(sketch, "E445.MirrorCS", {"start": v(332.5, -101.25) * mm, "end": v(332.5, -114.25) * mm});
            skLineSegment(sketch, "E446.MirrorCS", {"start": v(327.5, -60.25) * mm, "end": v(314.5, -60.25) * mm});
            skLineSegment(sketch, "E447.MirrorCS", {"start": v(309.5, -47.25) * mm, "end": v(309.5, -60.25) * mm});
            skLineSegment(sketch, "E448.MirrorCS", {"start": v(296.5, -96.25) * mm, "end": v(309.5, -96.25) * mm});
            skLineSegment(sketch, "E449.MirrorCS", {"start": v(363.5, -114.25) * mm, "end": v(350.5, -114.25) * mm});
            skLineSegment(sketch, "E450.MirrorCS", {"start": v(332.5, -114.25) * mm, "end": v(345.5, -114.25) * mm});
            skLineSegment(sketch, "E451.MirrorCS", {"start": v(327.5, -65.25) * mm, "end": v(327.5, -78.25) * mm});
            skLineSegment(sketch, "E452.MirrorCS", {"start": v(309.5, -29.25) * mm, "end": v(309.5, -42.25) * mm});
            skLineSegment(sketch, "E453.MirrorCS", {"start": v(345.5, -29.25) * mm, "end": v(345.5, -42.25) * mm});
            skLineSegment(sketch, "E454.MirrorCS", {"start": v(327.5, -47.25) * mm, "end": v(314.5, -47.25) * mm});
            skLineSegment(sketch, "E455.MirrorCS", {"start": v(309.5, -65.25) * mm, "end": v(309.5, -78.25) * mm});
            skLineSegment(sketch, "E456.MirrorCS", {"start": v(368.5, -114.25) * mm, "end": v(381.5, -114.25) * mm});
            skLineSegment(sketch, "E457.MirrorCS", {"start": v(296.5, -29.25) * mm, "end": v(296.5, -42.25) * mm});
            skLineSegment(sketch, "E458.MirrorCS", {"start": v(368.5, -101.25) * mm, "end": v(368.5, -114.25) * mm});
            skLineSegment(sketch, "E459.MirrorCS", {"start": v(332.5, -42.25) * mm, "end": v(345.5, -42.25) * mm});
            skLineSegment(sketch, "E460.MirrorCS", {"start": v(381.5, -119.25) * mm, "end": v(381.5, -132.25) * mm});
            skLineSegment(sketch, "E461.MirrorCS", {"start": v(363.5, -119.25) * mm, "end": v(350.5, -119.25) * mm});
            skLineSegment(sketch, "E462.MirrorCS", {"start": v(332.5, -96.25) * mm, "end": v(345.5, -96.25) * mm});
            skLineSegment(sketch, "E463.MirrorCS", {"start": v(363.5, -83.25) * mm, "end": v(350.5, -83.25) * mm});
            skLineSegment(sketch, "E464.MirrorCS", {"start": v(363.5, -42.25) * mm, "end": v(350.5, -42.25) * mm});
            skLineSegment(sketch, "E465.MirrorCS", {"start": v(314.5, -47.25) * mm, "end": v(314.5, -60.25) * mm});
            skLineSegment(sketch, "E466.MirrorCS", {"start": v(332.5, -78.25) * mm, "end": v(345.5, -78.25) * mm});
            skLineSegment(sketch, "E467.MirrorCS", {"start": v(296.5, -78.25) * mm, "end": v(309.5, -78.25) * mm});
            skLineSegment(sketch, "E468.MirrorCS", {"start": v(368.5, -29.25) * mm, "end": v(381.5, -29.25) * mm});
            skLineSegment(sketch, "E469.MirrorCS", {"start": v(332.5, -119.25) * mm, "end": v(332.5, -132.25) * mm});
            skLineSegment(sketch, "E470.MirrorCS", {"start": v(381.5, -65.25) * mm, "end": v(381.5, -78.25) * mm});
            skLineSegment(sketch, "E471.MirrorCS", {"start": v(296.5, -83.25) * mm, "end": v(309.5, -83.25) * mm});
            skLineSegment(sketch, "E472.MirrorCS", {"start": v(296.5, -29.25) * mm, "end": v(309.5, -29.25) * mm});
            skLineSegment(sketch, "E473.MirrorCS", {"start": v(327.5, -29.25) * mm, "end": v(327.5, -42.25) * mm});
            skLineSegment(sketch, "E474.MirrorCS", {"start": v(296.5, -47.25) * mm, "end": v(309.5, -47.25) * mm});
            skLineSegment(sketch, "E475.MirrorCS", {"start": v(368.5, -96.25) * mm, "end": v(381.5, -96.25) * mm});
            skLineSegment(sketch, "E476.MirrorCS", {"start": v(296.5, -42.25) * mm, "end": v(309.5, -42.25) * mm});
            skLineSegment(sketch, "E477.MirrorCS", {"start": v(368.5, -132.25) * mm, "end": v(381.5, -132.25) * mm});
            skLineSegment(sketch, "E478.MirrorCS", {"start": v(363.5, -119.25) * mm, "end": v(363.5, -132.25) * mm});
            skLineSegment(sketch, "E479.MirrorCS", {"start": v(363.5, -65.25) * mm, "end": v(350.5, -65.25) * mm});
            skLineSegment(sketch, "E480.MirrorCS", {"start": v(345.5, -65.25) * mm, "end": v(345.5, -78.25) * mm});
            skLineSegment(sketch, "E481.MirrorCS", {"start": v(363.5, -60.25) * mm, "end": v(350.5, -60.25) * mm});
            skLineSegment(sketch, "E482.MirrorCS", {"start": v(368.5, -83.25) * mm, "end": v(368.5, -96.25) * mm});
            skLineSegment(sketch, "E483.MirrorCS", {"start": v(350.5, -83.25) * mm, "end": v(350.5, -96.25) * mm});
            skLineSegment(sketch, "E484.MirrorCS", {"start": v(345.5, -119.25) * mm, "end": v(345.5, -132.25) * mm});
            skLineSegment(sketch, "E485.MirrorCS", {"start": v(296.5, -132.25) * mm, "end": v(309.5, -132.25) * mm});
            skLineSegment(sketch, "E486.MirrorCS", {"start": v(368.5, -78.25) * mm, "end": v(381.5, -78.25) * mm});
            skLineSegment(sketch, "E487.MirrorCS", {"start": v(363.5, -101.25) * mm, "end": v(363.5, -114.25) * mm});
            skLineSegment(sketch, "E488.MirrorCS", {"start": v(345.5, -101.25) * mm, "end": v(345.5, -114.25) * mm});
            skLineSegment(sketch, "E489.MirrorCS", {"start": v(363.5, -65.25) * mm, "end": v(363.5, -78.25) * mm});
            skLineSegment(sketch, "E490.MirrorCS", {"start": v(327.5, -29.25) * mm, "end": v(314.5, -29.25) * mm});
            skLineSegment(sketch, "E491.MirrorCS", {"start": v(327.5, -114.25) * mm, "end": v(314.5, -114.25) * mm});
            skCircle(sketch, "E492", {"center": v(32.44, -141.9) * mm, "radius": 1.5 * mm});
            skCircle(sketch, "E493", {"center": v(141.27, -141.9) * mm, "radius": 1.5 * mm});
            skCircle(sketch, "E494", {"center": v(248.81, -141.9) * mm, "radius": 1.5 * mm});
            skCircle(sketch, "E495", {"center": v(357.84, -141.9) * mm, "radius": 1.5 * mm});
            skCircle(sketch, "E496", {"center": v(32.44, -20) * mm, "radius": 1.5 * mm});
            skCircle(sketch, "E497", {"center": v(115, -20) * mm, "radius": 1.5 * mm});
            skCircle(sketch, "E498", {"center": v(248.81, -20) * mm, "radius": 1.5 * mm});
            skCircle(sketch, "E499", {"center": v(350.5, -20) * mm, "radius": 1.5 * mm});
            skSolve(sketch);
        }
        {
            var Q0;
            Q0=qSketchRegion(id+"F0",true);
            extrude(context, id + "F1", {"entities" : qUnion([Q0]), "depth" : 3 * mm});
        }
        {
            var Q0;
            Q0=qCreatedBy(makeId("Top.planeOp"),FACE);
            var sketch = newSketch(context, id + "F2", { "sketchPlane" : qUnion([Q0])});
            skLineSegment(sketch, "E500.bottom", {"start": v(0, 0) * mm, "end": v(390, 0) * mm});
            skLineSegment(sketch, "E500.top", {"start": v(0, -150) * mm, "end": v(390, -150) * mm});
            skLineSegment(sketch, "E500.left", {"start": v(0, 0) * mm, "end": v(0, -150) * mm});
            skLineSegment(sketch, "E500.right", {"start": v(390, 0) * mm, "end": v(390, -150) * mm});
            skCircle(sketch, "E501", {"center": v(32.44, -20) * mm, "radius": 1.5 * mm});
            skCircle(sketch, "E502", {"center": v(115, -20) * mm, "radius": 1.5 * mm});
            skCircle(sketch, "E503", {"center": v(248.81, -20) * mm, "radius": 1.5 * mm});
            skCircle(sketch, "E504", {"center": v(350.5, -20) * mm, "radius": 1.5 * mm});
            skCircle(sketch, "E505", {"center": v(32.44, -141.9) * mm, "radius": 1.5 * mm});
            skCircle(sketch, "E506", {"center": v(141.27, -141.9) * mm, "radius": 1.5 * mm});
            skCircle(sketch, "E507", {"center": v(248.81, -141.9) * mm, "radius": 1.5 * mm});
            skCircle(sketch, "E508", {"center": v(357.84, -141.9) * mm, "radius": 1.5 * mm});
            skSolve(sketch);
        }
        {
            var Q0;
            Q0=qSketchRegion(id+"F2",true);
            extrude(context, id + "F3", {"entities" : qUnion([Q0]), "oppositeDirection" : true, "depth" : 2 * mm});
        }
        {
            var Q0;
            Q0=qCreatedBy(makeId("Top.planeOp"),FACE);
            var sketch = newSketch(context, id + "F4", { "sketchPlane" : qUnion([Q0])});
            skLineSegment(sketch, "E509.bottom", {"start": v(0, 0) * mm, "end": v(390, 0) * mm});
            skLineSegment(sketch, "E509.top", {"start": v(0, -150) * mm, "end": v(390, -150) * mm});
            skLineSegment(sketch, "E509.left", {"start": v(0, 0) * mm, "end": v(0, -150) * mm});
            skLineSegment(sketch, "E509.right", {"start": v(390, 0) * mm, "end": v(390, -150) * mm});
            skLineSegment(sketch, "E510.bottom", {"start": v(2, -2) * mm, "end": v(388, -2) * mm});
            skLineSegment(sketch, "E510.top", {"start": v(2, -148) * mm, "end": v(388, -148) * mm});
            skLineSegment(sketch, "E510.left", {"start": v(2, -2) * mm, "end": v(2, -148) * mm});
            skLineSegment(sketch, "E510.right", {"start": v(388, -2) * mm, "end": v(388, -148) * mm});
            skSolve(sketch);
        }
        {
            var Q0;
            Q0=qSketchRegion(id+"F4",true);
            extrude(context, id + "F5", {"entities" : qUnion([Q0]), "oppositeDirection" : true, "depth" : 250 * mm});
        }
    });
